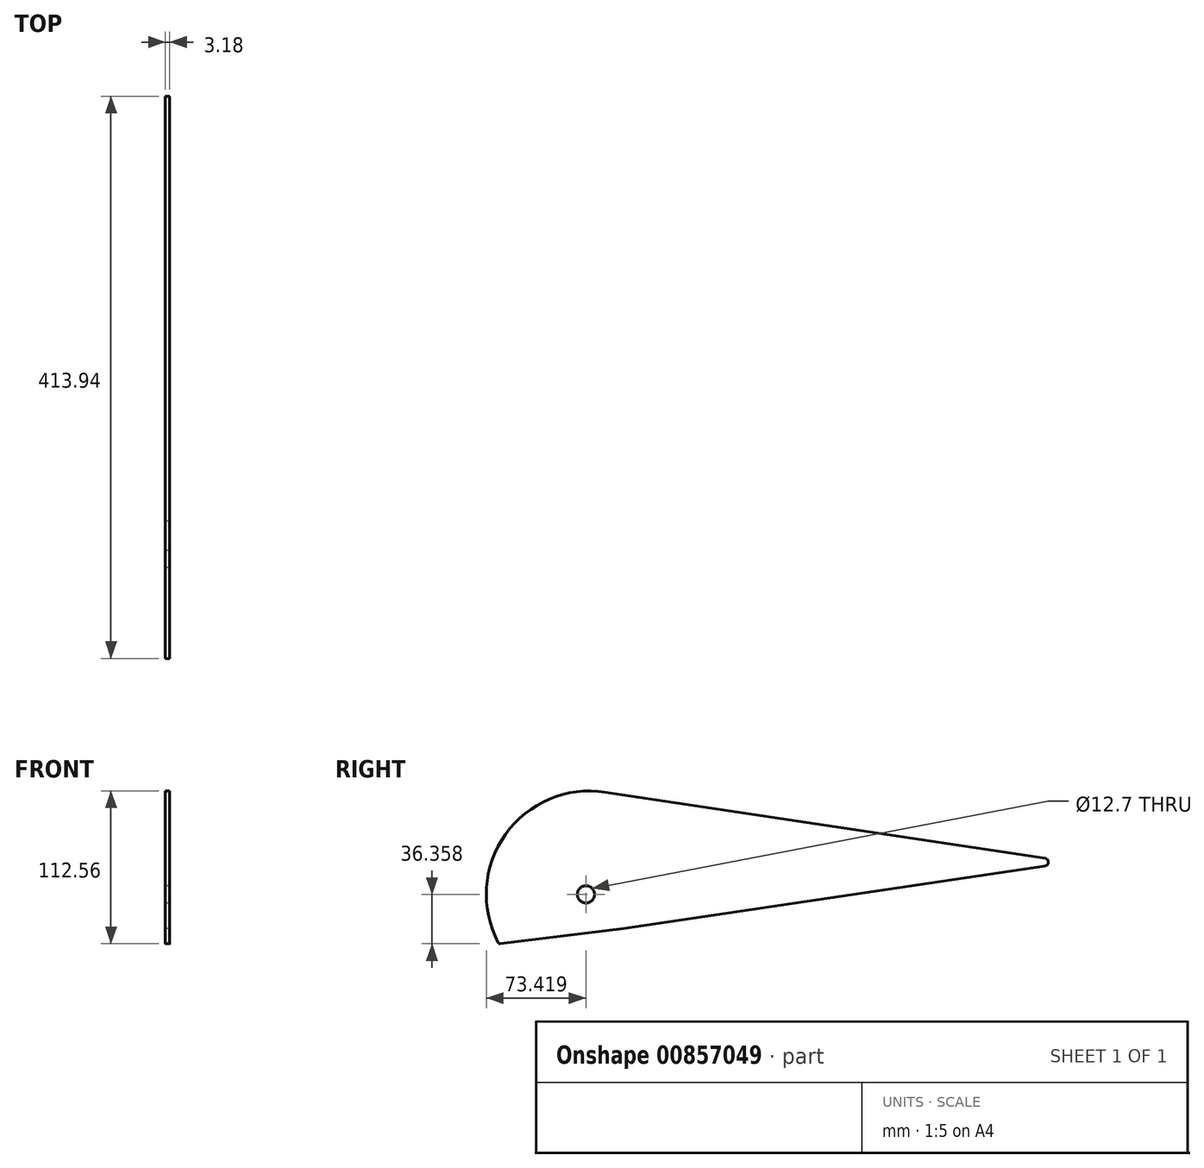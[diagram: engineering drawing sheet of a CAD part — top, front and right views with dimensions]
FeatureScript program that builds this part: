
annotation { "Feature Type Name" : "Feature", "Feature Type Description" : "" }
export const myFeature = defineFeature(function(context is Context, id is Id, definition is map)
    precondition{}
    {
        {
            var Q0;
            Q0=qCreatedBy(makeId("Right.planeOp"),FACE);
            var sketch = newSketch(context, id + "F0", { "sketchPlane" : qUnion([Q0])});
            skCircle(sketch, "E0", {"center": v(309.96, 0) * mm, "radius": 2.78 * mm});
            skLineSegment(sketch, "E1", {"start": v(0, -48.82) * mm, "end": v(310.37, -2.75) * mm});
            skPoint(sketch, "E2", {"position": v(-25, -23.81) * mm});
            skCircle(sketch, "E3", {"center": v(-25, -23.81) * mm, "radius": 76.2 * mm});
            skLineSegment(sketch, "E4", {"start": v(-101.2, -23.81) * mm, "end": v(-101.2, -74.61) * mm});
            skLineSegment(sketch, "E5", {"start": v(0, -48.82) * mm, "end": v(-101.2, -61.46) * mm});
            skLineSegment(sketch, "E6", {"start": v(0, -48.82) * mm, "end": v(-101.2, -63.84) * mm});
            skLineSegment(sketch, "E7", {"start": v(-13.66, 51.54) * mm, "end": v(310.37, 2.75) * mm});
            skCircle(sketch, "E8", {"center": v(-27.78, -23.81) * mm, "radius": 6.35 * mm});
            skLineSegment(sketch, "E9.bottom", {"start": v(0, -48.82) * mm, "end": v(3.18, -48.82) * mm});
            skLineSegment(sketch, "E9.top", {"start": v(0, -23.42) * mm, "end": v(3.17, -23.42) * mm});
            skLineSegment(sketch, "E9.left", {"start": v(0, -48.82) * mm, "end": v(0, -23.42) * mm});
            skLineSegment(sketch, "E9.right", {"start": v(3.18, -48.82) * mm, "end": v(3.17, -23.42) * mm});
            skPoint(sketch, "E10", {"position": v(3.18, -48.34) * mm});
            skSolve(sketch);
        }
        {
            var Q0;
            Q0=makeQuery(id+"F0.imprint","IMPRINT",FACE,{"disambiguationData":[TD([[makeQuery(id+"F0.imprint","IMPRINT",EDGE,{"derivedFrom":sQuery(id+"F0.wireOp",EDGE,"E8")}),-1.0]])]});
            var Q1;
            {var subQ3=sQuery(id+"F0.wireOp",EDGE,"E7");Q1=makeQuery(id+"F0.imprint","IMPRINT",FACE,{"disambiguationData":[TD([[makeQuery(id+"F0.imprint","IMPRINT",EDGE,{"derivedFrom":subQ3}),-1.0]])]});}
            var Q2;
            {var subQ0=sQuery(id+"F0.wireOp",EDGE,"E0");var subQ1=makeQuery(id+"F0.imprint","INTERSECT",VERTEX,{"derivedFrom":[subQ0,sQuery(id+"F0.wireOp",EDGE,"E1")]});Q2=makeQuery(id+"F0.imprint","IMPRINT",FACE,{"disambiguationData":[TD([[makeQuery(id+"F0.imprint","IMPRINT",EDGE,{"disambiguationData":[TD([[subQ1,1.0]])],"derivedFrom":subQ0}),1.0]])]});}
            var Q3;
            {var subQ4=sQuery(id+"F0.wireOp",EDGE,"E9.top");Q3=makeQuery(id+"F0.imprint","IMPRINT",FACE,{"disambiguationData":[TD([[makeQuery(id+"F0.imprint","IMPRINT",EDGE,{"derivedFrom":subQ4}),-1.0]])]});}
            extrude(context, id + "F1", {"entities" : qUnion([Q0, Q1, Q2, Q3]), "depth" : 3.17 * mm, "offsetDistance" : 25.4 * mm, "symmetric" : true});
        }
        {
            var Q0;
            Q0=makeQuery(id+"F1.opExtrude","SWEPT_EDGE",EDGE,{"disambiguationData":[OSD([sQuery(id+"F0.wireOp",EDGE,"E3"),sQuery(id+"F0.wireOp",EDGE,"E5")])]});
            fillet(context, id + "F2", {"entities" : qUnion([Q0]), "radius" : 1.59 * mm, "tangentPropagation" : true, "allowEdgeOverflow" : false});
        }
    });
